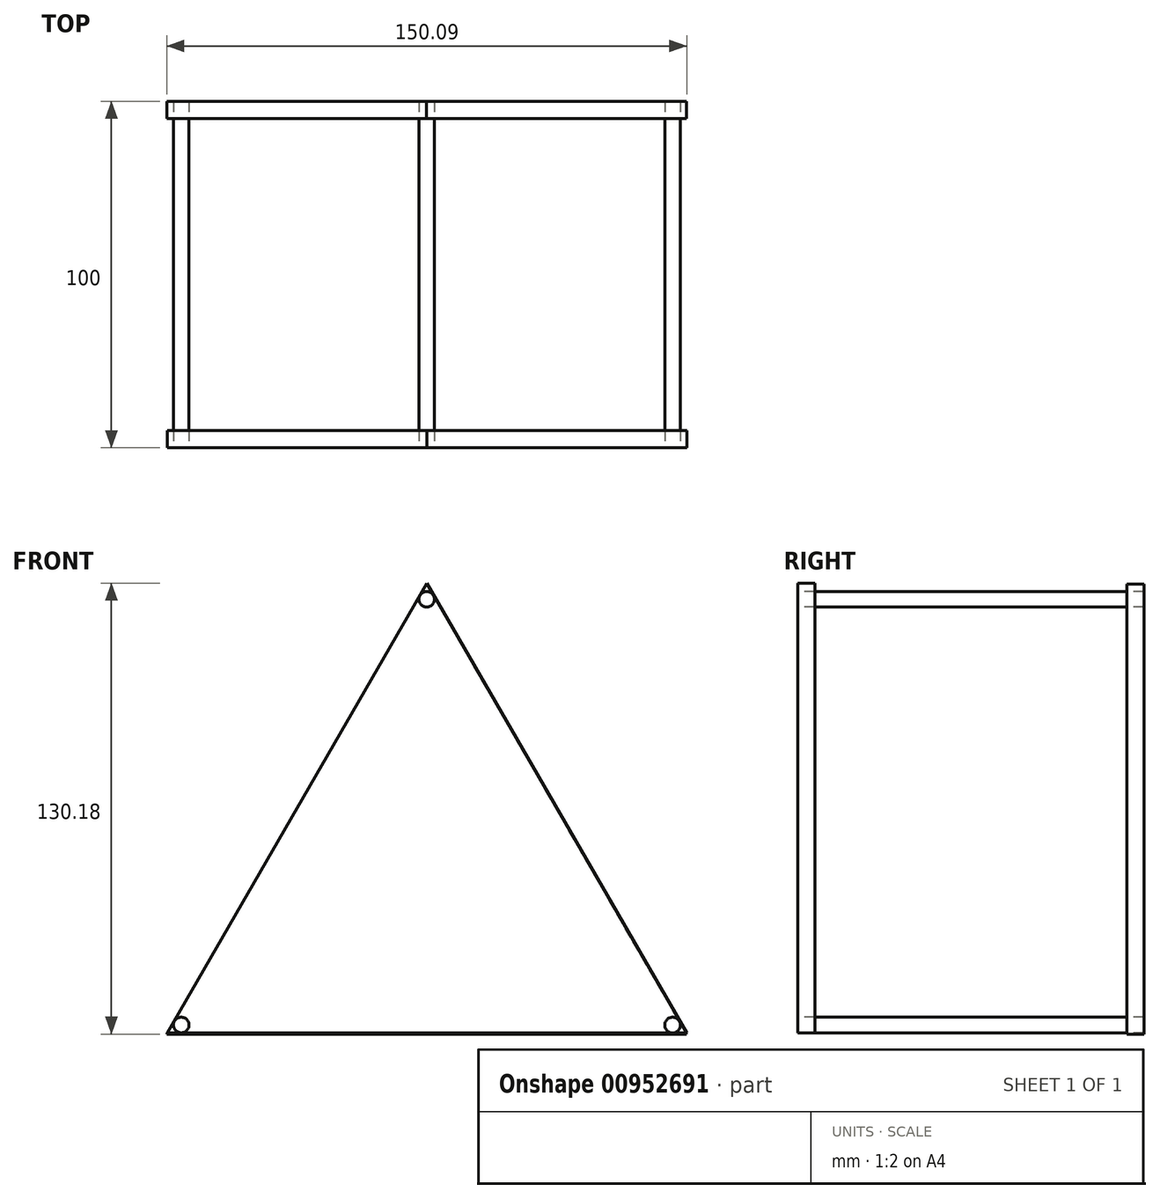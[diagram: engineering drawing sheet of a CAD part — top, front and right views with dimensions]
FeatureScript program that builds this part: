
annotation { "Feature Type Name" : "Feature", "Feature Type Description" : "" }
export const myFeature = defineFeature(function(context is Context, id is Id, definition is map)
    precondition{}
    {
        {
            var Q0;
            Q0=qCreatedBy(makeId("Front.planeOp"),FACE);
            cPlane(context, id + "F0", {"entities" : qUnion([Q0]), "cplaneType" : CPlaneType.OFFSET, "offset" : 50 * mm, "width" : 150 * mm, "height" : 150 * mm});
        }
        {
            var Q0;
            Q0=qCreatedBy(makeId("Front.planeOp"),FACE);
            cPlane(context, id + "F1", {"entities" : qUnion([Q0]), "cplaneType" : CPlaneType.OFFSET, "offset" : 50 * mm, "oppositeDirection" : true, "width" : 150 * mm, "height" : 150 * mm});
        }
        {
            var Q0;
            Q0=qCreatedBy(id+"F0.planeOp",FACE);
            var sketch = newSketch(context, id + "F2", { "sketchPlane" : qUnion([Q0])});
            skLineSegment(sketch, "E0", {"start": v(-75.04, -42.93) * mm, "end": v(74.96, -42.93) * mm});
            skLineSegment(sketch, "E1", {"start": v(-75.04, -42.93) * mm, "end": v(-0.04, 86.98) * mm});
            skLineSegment(sketch, "E2", {"start": v(74.96, -42.93) * mm, "end": v(-0.04, 86.98) * mm});
            skSolve(sketch);
        }
        {
            var Q0;
            Q0=qCreatedBy(id+"F1.planeOp",FACE);
            var sketch = newSketch(context, id + "F3", { "sketchPlane" : qUnion([Q0])});
            skLineSegment(sketch, "E3", {"start": v(-75.13, -43.2) * mm, "end": v(74.87, -43.2) * mm});
            skLineSegment(sketch, "E4", {"start": v(-75.13, -43.2) * mm, "end": v(-0.13, 86.7) * mm});
            skLineSegment(sketch, "E5", {"start": v(74.87, -43.2) * mm, "end": v(-0.13, 86.7) * mm});
            skSolve(sketch);
        }
        {
            var Q0;
            Q0=makeQuery(id+"F2.imprint","IMPRINT",FACE,{"disambiguationData":[TD([[makeQuery(id+"F2.imprint","IMPRINT",EDGE,{"derivedFrom":sQuery(id+"F2.wireOp",EDGE,"E0")}),1.0]])]});
            extrude(context, id + "F4", {"entities" : qUnion([Q0]), "oppositeDirection" : true, "depth" : 5 * mm, "offsetDistance" : 25 * mm});
        }
        {
            var Q0;
            Q0=makeQuery(id+"F3.imprint","IMPRINT",FACE,{"disambiguationData":[TD([[makeQuery(id+"F3.imprint","IMPRINT",EDGE,{"derivedFrom":sQuery(id+"F3.wireOp",EDGE,"E3")}),1.0]])]});
            extrude(context, id + "F5", {"entities" : qUnion([Q0]), "depth" : 5 * mm, "offsetDistance" : 25 * mm});
        }
        {
            var Q0;
            Q0=qCreatedBy(id+"F0.planeOp",FACE);
            var sketch = newSketch(context, id + "F6", { "sketchPlane" : qUnion([Q0])});
            skCircle(sketch, "E6", {"center": v(-0.1, 82.28) * mm, "radius": 2.24 * mm});
            skPoint(sketch, "E6.first.point", {"position": v(0, 80.04) * mm});
            skPoint(sketch, "E6.second.point", {"position": v(-2.32, 82.08) * mm});
            skPoint(sketch, "E6.third.point", {"position": v(2.13, 82.52) * mm});
            skCircle(sketch, "E7", {"center": v(-70.97, -40.57) * mm, "radius": 2.25 * mm});
            skPoint(sketch, "E7.first.point", {"position": v(-68.86, -39.79) * mm});
            skPoint(sketch, "E7.second.point", {"position": v(-70.79, -42.82) * mm});
            skPoint(sketch, "E7.third.point", {"position": v(-72.98, -39.57) * mm});
            skCircle(sketch, "E8", {"center": v(70.87, -40.6) * mm, "radius": 2.26 * mm});
            skPoint(sketch, "E8.first.point", {"position": v(68.9, -39.5) * mm});
            skPoint(sketch, "E8.second.point", {"position": v(72, -38.64) * mm});
            skPoint(sketch, "E8.third.point", {"position": v(69.41, -42.32) * mm});
            skSolve(sketch);
        }
        {
            var Q0;
            Q0=makeQuery(id+"F6.imprint","IMPRINT",FACE,{"disambiguationData":[TD([[makeQuery(id+"F6.imprint","IMPRINT",EDGE,{"derivedFrom":sQuery(id+"F6.wireOp",EDGE,"E6")}),1.0]])]});
            var Q1;
            Q1=makeQuery(id+"F6.imprint","IMPRINT",FACE,{"disambiguationData":[TD([[makeQuery(id+"F6.imprint","IMPRINT",EDGE,{"derivedFrom":sQuery(id+"F6.wireOp",EDGE,"E7")}),1.0]])]});
            var Q2;
            Q2=makeQuery(id+"F6.imprint","IMPRINT",FACE,{"disambiguationData":[TD([[makeQuery(id+"F6.imprint","IMPRINT",EDGE,{"derivedFrom":sQuery(id+"F6.wireOp",EDGE,"E8")}),1.0]])]});
            extrude(context, id + "F7", {"entities" : qUnion([Q0, Q1, Q2]), "oppositeDirection" : true, "depth" : 100 * mm, "offsetDistance" : 25 * mm});
        }
    });
